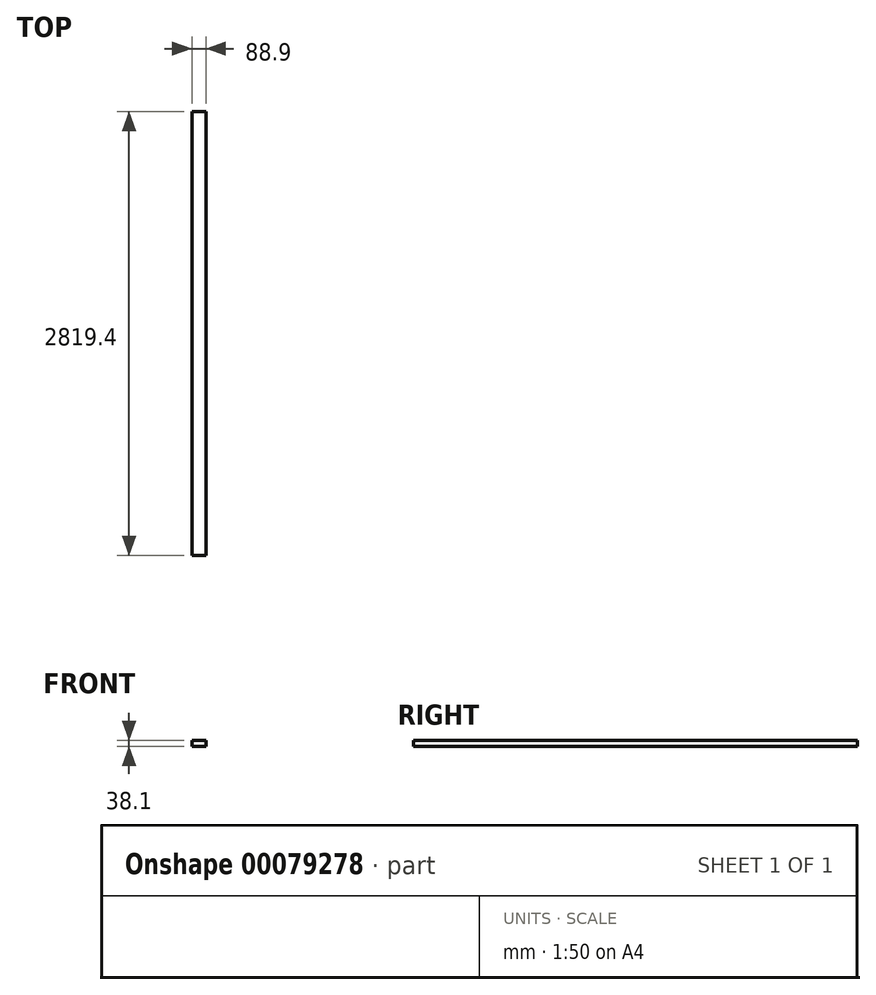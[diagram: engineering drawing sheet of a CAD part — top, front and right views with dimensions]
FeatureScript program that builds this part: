
annotation { "Feature Type Name" : "Feature", "Feature Type Description" : "" }
export const myFeature = defineFeature(function(context is Context, id is Id, definition is map)
    precondition{}
    {
        {
            var Q0;
            Q0=qCreatedBy(makeId("Front.planeOp"),FACE);
            var sketch = newSketch(context, id + "F0", { "sketchPlane" : qUnion([Q0])});
            skLineSegment(sketch, "E0.bottom", {"start": v(44.45, 19.05) * mm, "end": v(-44.45, 19.05) * mm});
            skLineSegment(sketch, "E0.top", {"start": v(44.45, -19.05) * mm, "end": v(-44.45, -19.05) * mm});
            skLineSegment(sketch, "E0.left", {"start": v(44.45, 19.05) * mm, "end": v(44.45, -19.05) * mm});
            skLineSegment(sketch, "E0.right", {"start": v(-44.45, 19.05) * mm, "end": v(-44.45, -19.05) * mm});
            skPoint(sketch, "E0.middle", {"position": v(0, 0) * mm});
            skSolve(sketch);
        }
        {
            var Q0;
            Q0 = qSketchRegion(id + "F0", true);
            extrude(context, id + "F1", {"entities" : qUnion([Q0]), "endBound" : BoundingType.SYMMETRIC, "depth" : 2819.4 * mm, "hasSecondDirection" : true, "secondDirectionOppositeDirection" : true, "secondDirectionDepth" : 25.4 * mm});
        }
    });
